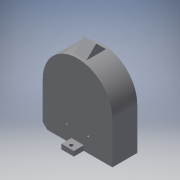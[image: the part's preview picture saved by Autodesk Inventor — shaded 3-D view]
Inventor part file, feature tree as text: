
AUTODESK INVENTOR PART (.ipt)
format: ipt  version: 2016 (Build 200138000, 138)  size: 164,864 bytes
history: native  units: in
note: dims shown in document units (in); Inventor stores cm internally (conversion verified against a paired STEP export)
features: extrude x7, sketch x7, reference x4, plane x1
ambient origin geometry x8: Origin, YZ Plane, XZ Plane, XY Plane, X Axis, Y Axis, Z Axis, Center Point
bodies: Solid1 (feature_tree)
feature tree (19):
  extrude  "Extrusion1"  Depth=1.0in TaperAngle=0.0deg
  extrude  "Extrusion2"  Depth=0.4in TaperAngle=0.0deg
  extrude  "Extrusion4"  Depth=0.1065in
  plane  "Work Plane1"
  extrude  "Extrusion7"  Depth=0.394in
  extrude  "Extrusion9"  Depth=0.5in TaperAngle=0.0deg
  extrude  "Extrusion10"  Depth=0.5in
  extrude  "Extrusion11"  Depth=1.0in
  sketch  "Sketch1"  dims[d0=2.8in d1=1.0in d2=0.0in]
  reference  "Reference1"
  sketch  "Sketch2"  dims[d4=0.4in d5=0.0in d13=0.4in d14=0.0in]
  reference  "Reference2"
  sketch  "Sketch4"  dims[d26=-1.4in d27=0.1065in]
  sketch  "Sketch7"  dims[d28=0.787in d29=0.394in]
  sketch  "Sketch9"  dims[d30=0.394in d31=0.5in d32=0.0in]
  sketch  "Sketch10"  dims[d39=0.25in d40=0.5in]
  sketch  "Sketch11"  dims[d41=0.15in d42=0.138in d43=1.0in d44=0.0in d45=0.25in d46=0.5in d47=0.15in d48=0.177in d49=1.0in d50=0.0in d51=0.5in d52=0.5in d53=0.0394in d54=0.098in d55=0.0394in d56=0.098in d57=1.0in d58=0.0in]
  reference  "Reference3"
  reference  "Reference4"
